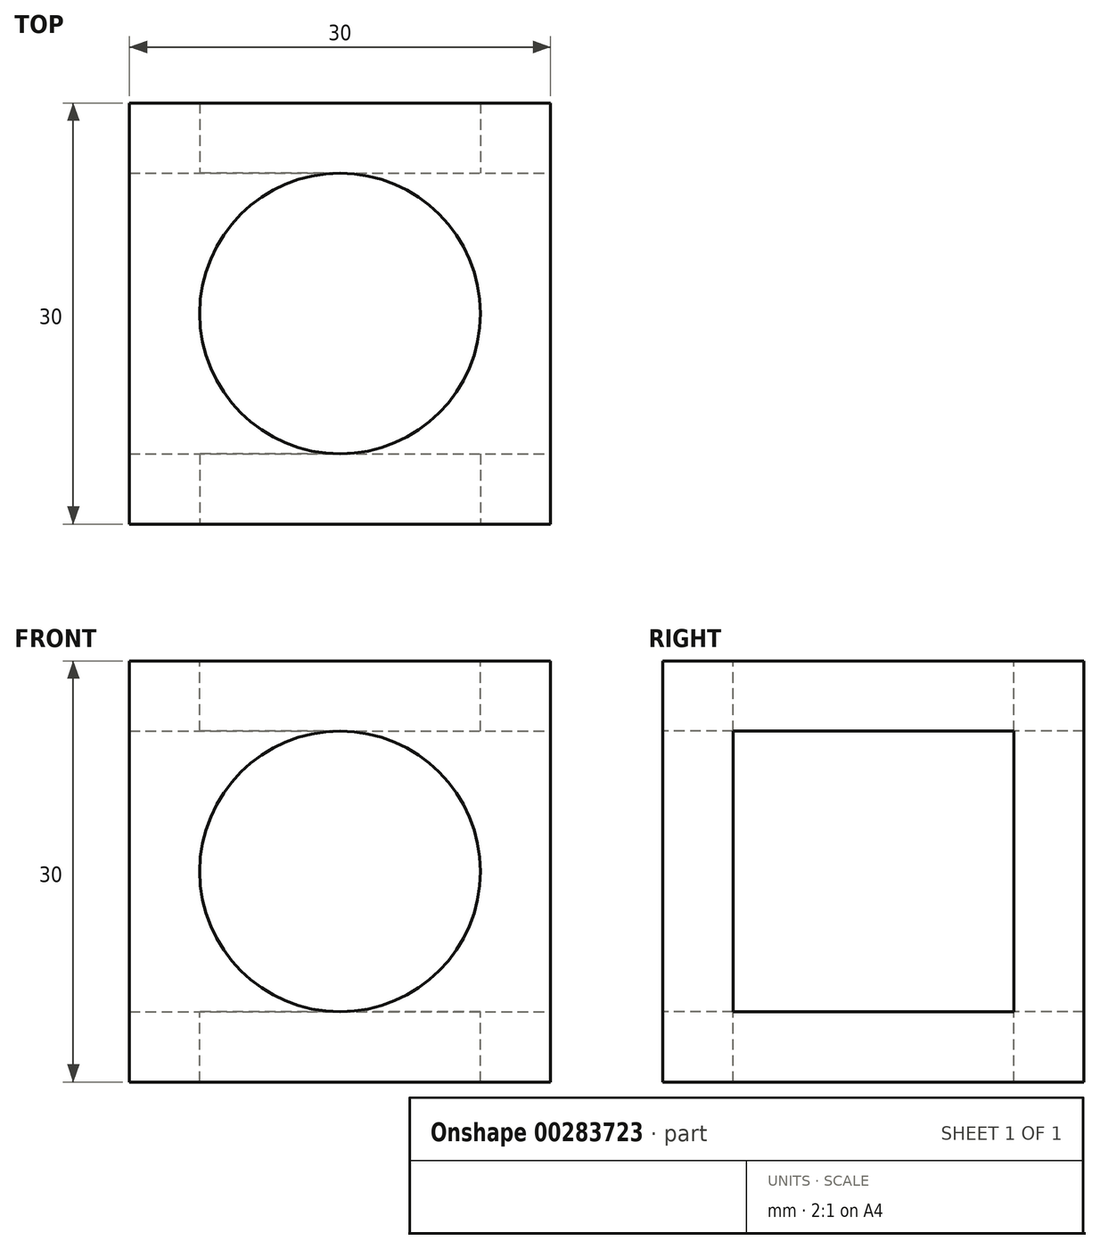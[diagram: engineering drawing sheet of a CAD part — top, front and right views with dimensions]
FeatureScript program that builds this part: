
annotation { "Feature Type Name" : "Feature", "Feature Type Description" : "" }
export const myFeature = defineFeature(function(context is Context, id is Id, definition is map)
    precondition{}
    {
        {
            var Q0;
            Q0=qCreatedBy(makeId("Front.planeOp"),FACE);
            var sketch = newSketch(context, id + "F0", { "sketchPlane" : qUnion([Q0])});
            skLineSegment(sketch, "E0.bottom", {"start": v(-15, 15) * mm, "end": v(15, 15) * mm});
            skLineSegment(sketch, "E0.top", {"start": v(-15, -15) * mm, "end": v(15, -15) * mm});
            skLineSegment(sketch, "E0.left", {"start": v(-15, 15) * mm, "end": v(-15, -15) * mm});
            skLineSegment(sketch, "E0.right", {"start": v(15, 15) * mm, "end": v(15, -15) * mm});
            skPoint(sketch, "E0.middle", {"position": v(0, 0) * mm});
            skSolve(sketch);
        }
        {
            var Q0;
            Q0=makeQuery(id+"F0.imprint","IMPRINT",FACE,{"disambiguationData":[TD([[makeQuery(id+"F0.imprint","IMPRINT",EDGE,{"derivedFrom":sQuery(id+"F0.wireOp",EDGE,"E0.bottom")}),-1.0]])]});
            extrude(context, id + "F1", {"entities" : qUnion([Q0]), "endBound" : BoundingType.SYMMETRIC, "depth" : 30 * mm});
        }
        {
            var Q0;
            Q0=makeQuery(id+"F1.opExtrude","CAP_FACE",FACE,{"disambiguationData":[OSD([sQuery(id+"F0.wireOp",EDGE,"E0.bottom"),sQuery(id+"F0.wireOp",EDGE,"E0.top"),sQuery(id+"F0.wireOp",EDGE,"E0.left"),sQuery(id+"F0.wireOp",EDGE,"E0.right")])],"isStart":false});
            var sketch = newSketch(context, id + "F2", { "sketchPlane" : qUnion([Q0])});
            skCircle(sketch, "E1", {"center": v(0, 0) * mm, "radius": 10 * mm});
            skSolve(sketch);
        }
        {
            var Q0;
            Q0 = qSketchRegion(id + "F2", true);
            extrude(context, id + "F3", {"entities" : qUnion([Q0]), "operationType" : NewBodyOperationType.REMOVE, "oppositeDirection" : true, "depth" : 30 * mm});
        }
        {
            var Q0;
            Q0=makeQuery(id+"F1.opExtrude","SWEPT_FACE",FACE,{"disambiguationData":[OSD([sQuery(id+"F0.wireOp",EDGE,"E0.bottom")])]});
            var sketch = newSketch(context, id + "F4", { "sketchPlane" : qUnion([Q0])});
            skCircle(sketch, "E2", {"center": v(0, 0) * mm, "radius": 10 * mm});
            skSolve(sketch);
        }
        {
            var Q0;
            Q0 = qSketchRegion(id + "F4", true);
            extrude(context, id + "F5", {"entities" : qUnion([Q0]), "operationType" : NewBodyOperationType.REMOVE, "oppositeDirection" : true, "depth" : 30 * mm});
        }
        {
            var Q0;
            Q0=makeQuery(id+"F1.opExtrude","SWEPT_FACE",FACE,{"disambiguationData":[OSD([sQuery(id+"F0.wireOp",EDGE,"E0.right")])]});
            var sketch = newSketch(context, id + "F6", { "sketchPlane" : qUnion([Q0])});
            skLineSegment(sketch, "E3.bottom", {"start": v(-10, 10) * mm, "end": v(10, 10) * mm});
            skLineSegment(sketch, "E3.top", {"start": v(-10, -10) * mm, "end": v(10, -10) * mm});
            skLineSegment(sketch, "E3.left", {"start": v(-10, 10) * mm, "end": v(-10, -10) * mm});
            skLineSegment(sketch, "E3.right", {"start": v(10, 10) * mm, "end": v(10, -10) * mm});
            skPoint(sketch, "E3.middle", {"position": v(0, 0) * mm});
            skSolve(sketch);
        }
        {
            var Q0;
            Q0 = qSketchRegion(id + "F6", true);
            extrude(context, id + "F7", {"entities" : qUnion([Q0]), "operationType" : NewBodyOperationType.REMOVE, "oppositeDirection" : true, "depth" : 30 * mm});
        }
    });
